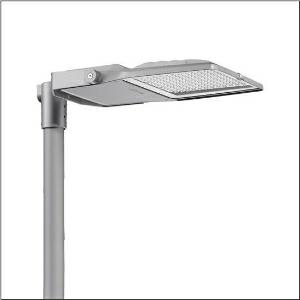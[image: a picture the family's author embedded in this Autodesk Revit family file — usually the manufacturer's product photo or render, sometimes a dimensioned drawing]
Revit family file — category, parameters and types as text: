
# Revit family: floodlight_fl_21_iq_midi___pl61_5xa7782f2c3a_b633
name_source: partatom
category: Lighting Fixtures
units: mm (PartAtom-declared; Revit-internal decimal feet)

## family parameters
Cut with Voids When Loaded = No
Host = Face
Light Source = No
Part Type = Normal
Room Calculation Point = No
Round Connector Dimension = Use Diameter
Shared = No

## types (1)
- --- (1 x LED, 35100 lm, 270.2 W, 3000K)
    Apparent Load = 270 VA
    CIE Flux Codes = 33 65 98 100 100
    Color Rendering = 70
    Color Temperature = 3000K
    Default Elevation = 1800 mm
    Description = Floodlight FL 21 iQ midi, floodlight, primary light control with lens, of PMMA, primary optical cover: protective disc, of toughened safety glass, transparent, light distribution: PL61, light emission: direct distribution, installation type: surface-mounted, LED, High Power LED, rated luminous flux: 35.100lm, luminous efficacy: 130lm/W, light colour: 730, colour temperature: 3000K, control gear: iQ Street-Remote/DALI, control: optimised constant luminous flux control (CLO 2.0), Desk-Remote (wireless, voltage-free reading and setting of iQ features in the workshop via application-optimized NFC function/RFID function), Smart-Wire, Night-Set, Temp-Guard, Auto-Match, Street-Remote, with terminal, 6-pole, mains connection: 220..240V, AC, 50/60Hz, start of lifetime: 270W, end of service life: 287W, reduction: 117W, luminaire housing, of diecast aluminium, powder-coated, Siteco® metallic grey (DB 702S), corrosivity category C5 mid according to DIN EN ISO 12944, suitable for swimming pools, chlorine-resistant, sealing non-destructively replaceable, please order mast flange separately, mast bracket, of steel, galvanised, powder-coated, Siteco® metallic grey (DB 702S), protection rating (complete): IP66, insulation class (complete): insulation class II (safety insulation), certification: CE, ENEC, VDE, protection symbol: D, impact resistance: IK08, permissible operating ambient temperature: -40..+40°C, permissible operating ambient temperature for outdoor applications: -40..+50°C, standard: DIN EN 12944, LABS conformity tested according to VDMA 24364:2018-05, packaging unit: 1 piece

Light Distribution: PL61
    Height = 76 mm
    Lamp = 1 x LED
    Lamp Light Flux = 35100 lm
    Lamp Power = 270.2 W
    Lamp count = 1
    Length = 657 mm
    Luminous efficacy = 130 lm/W
    Manufacturer = Siteco
    ModVariant = No
    Model = 5XA7782F2C3A
    Number of Poles = 1
    OnlyDefault = Yes
    Power Factor = 1
    Product Name = Floodlight FL 21 iQ midi | PL61
    Product group = floodlight | pylon annexe
    ProductGroupID = 6200
    Protection Class = Protection class II
    Protection Degree = IP 66
    RLX_Detail_Level = 1
    RLX_Emergency_Light_Flux = 0 lm
    RLX_Emergency_Type = 0
    RLX_Emergency_Type_DB = No
    RlxData = <blob elided: 153493 chars, md5=247f1324>
    Socket = socket
    Standby Power = 0 W
    System Light Flux = 35100 lm
    System Power = 270 W
    Type Comments = factory setting: luminous flux: 100 % | dim-lin: 254 | 620 mA
    Type Image = l_1007123.jpg
    URL = http://relux.com
    VarID = @adj_108298
    Voltage = 0 V
    Weight = 0.00 kg
    Width = 442 mm

## geometry (parser evidence)
native form markers: Blend x4, Sweep x13
no freeform markers — native parametric forms only
